# Revit family: Faucet-Kitchen-Grohe-LadyLux-33893_Series
name_source: partatom
category: Plumbing Fixtures
revit_build: Autodesk Revit 2014 (Build: 20130308_1515(x64)
units: mm (PartAtom-declared; Revit-internal decimal feet)

## types (2) — shared parameters
ADA Compliant = Yes
Assembly Code = D2020300
CW Connection = Yes
CWFU = 3
CalGreen Compliant = Yes
Cold Water Connection Diameter = 3/8"
Default Elevation = 0"
Description = LadyLux Single-Handle Kitchen Faucet
Flow Rate = 1.75 gpm (6.6 L/min)
HW Connection = Yes
HWFU = 3
Height = 14 15/16"
Hot Water Connection Diameter = 0"
Installation Type = Deck-Mounted
Length = 8 1/16"
Manufacturer = Grohe
Price = Prices may vary. Please consult Manufacturer Representative for most up-to-date price list.
URL = https://www.grohe.us
Vent Connection = No
WFU = 4
Warranty Documentation Link = https://cdn.cloud.grohe.com
Waste Connection = No
cUPC Compliant = Yes

## per-type parameters (varying)
| type | Finish | Material | Shipping Weight |
| 33893002 | Brass-Grohe-002-StarLight Chrome | Brass-Grohe-002-StarLight Chrome | 6.36 lb |
| 33893DC2 | Brass-Grohe-DC2-SuperSteel | Brass-Grohe-DC2-SuperSteel | 6.71 lb |

note: column(s) folded — value = type name in every type: Model

## geometry (parser evidence)
native form markers: Sweep x1
no freeform markers — native parametric forms only
